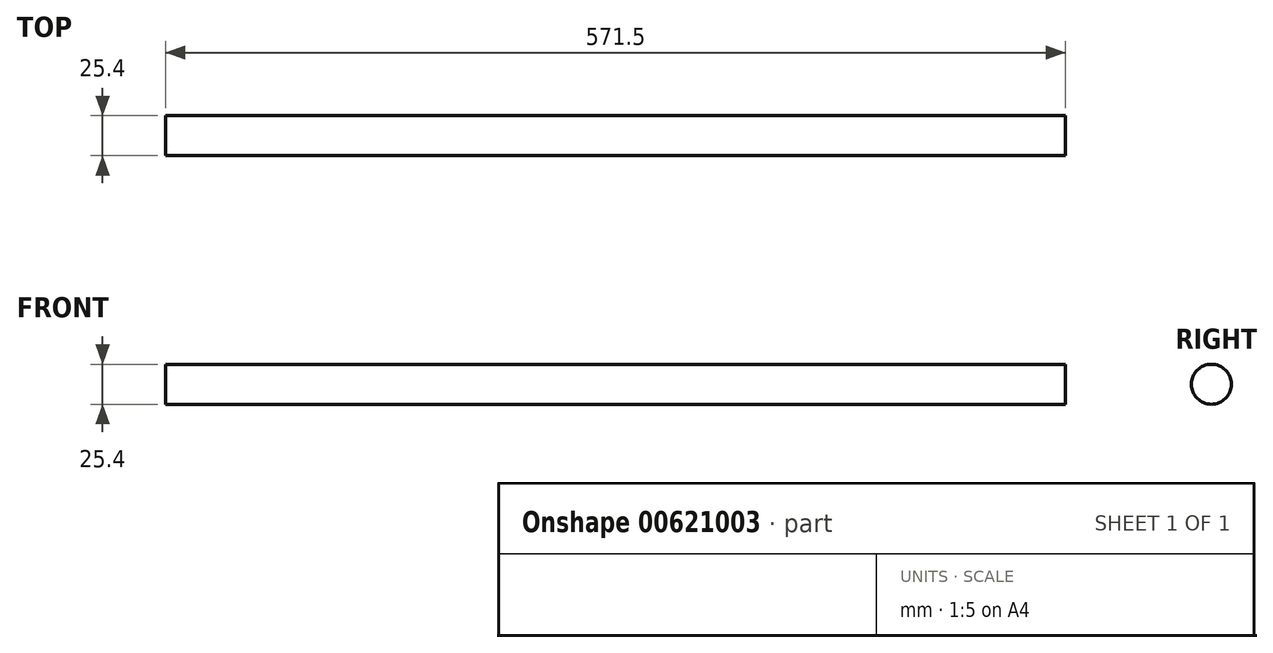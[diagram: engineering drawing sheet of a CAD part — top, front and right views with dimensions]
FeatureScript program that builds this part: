
annotation { "Feature Type Name" : "Feature", "Feature Type Description" : "" }
export const myFeature = defineFeature(function(context is Context, id is Id, definition is map)
    precondition{}
    {
        {
            var Q0;
            Q0=qCreatedBy(makeId("Right.planeOp"),FACE);
            var sketch = newSketch(context, id + "F0", { "sketchPlane" : qUnion([Q0])});
            skCircle(sketch, "E0", {"center": v(0, 0) * mm, "radius": 12.7 * mm});
            skSolve(sketch);
        }
        {
            var Q0;
            Q0 = qSketchRegion(id + "F0", true);
            extrude(context, id + "F1", {"entities" : qUnion([Q0]), "depth" : 571.5 * mm, "offsetDistance" : 25.4 * mm});
        }
    });
